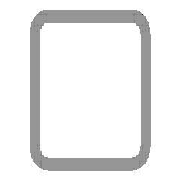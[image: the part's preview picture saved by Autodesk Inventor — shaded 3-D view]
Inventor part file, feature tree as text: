
AUTODESK INVENTOR PART (.ipt)
format: ipt  version: 2025.1 (Build 291241020, 241B)  size: 134,656 bytes
history: native  units: mm (DEFAULTED — no unit token found)
features: other x4, sketch x1, plane x1
ambient origin geometry x8: Origin, YZ Plane, XZ Plane, XY Plane, X Axis, Y Axis, Z Axis, Center Point
bodies: Solid1 (feature_tree), Body (feature_tree)
feature tree (6):
  parser-record x1  (decoder bookkeeping rows leaked as tree rows — omitted from the tree; the rows remain in map.json)
  other  "Driven Length"
  other  "Start Plane"
  other  "End Plane"
  sketch  "Sketch3"  dims[d3=1350.0mm d4=0.0mm d7=8.0mm d9=100.0mm d11=100.0mm d12=4.0mm d13=50.0mm d14=1400.0mm d15=50.0mm d16=50.0mm d17=90.0deg d18=1350.0mm]
  plane  "Work Plane3"
